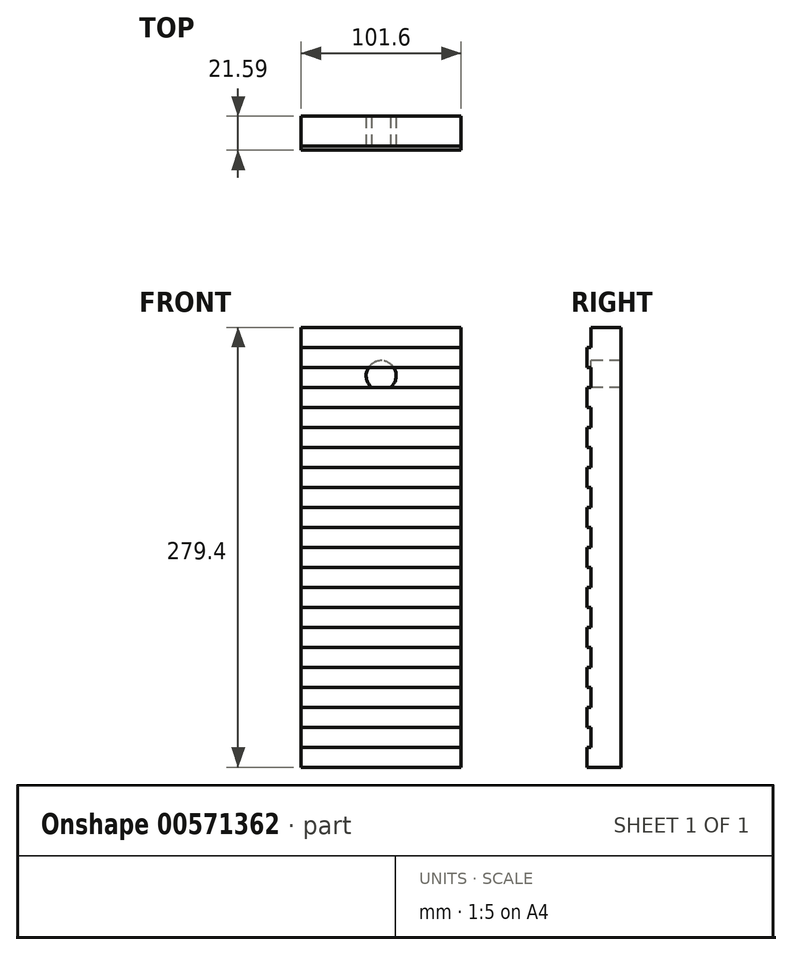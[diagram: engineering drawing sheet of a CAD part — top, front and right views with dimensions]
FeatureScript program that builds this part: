
annotation { "Feature Type Name" : "Feature", "Feature Type Description" : "" }
export const myFeature = defineFeature(function(context is Context, id is Id, definition is map)
    precondition{}
    {
        {
            var Q0;
            Q0=qCreatedBy(makeId("Front.planeOp"),FACE);
            var sketch = newSketch(context, id + "F0", { "sketchPlane" : qUnion([Q0])});
            skLineSegment(sketch, "E0", {"start": v(-129.55, 107.06) * mm, "end": v(-27.95, 107.06) * mm});
            skLineSegment(sketch, "E1", {"start": v(-27.95, 107.06) * mm, "end": v(-27.95, -172.34) * mm});
            skLineSegment(sketch, "E2", {"start": v(-27.95, -172.34) * mm, "end": v(-129.55, -172.34) * mm});
            skLineSegment(sketch, "E3", {"start": v(-129.55, 107.06) * mm, "end": v(-129.55, -172.34) * mm});
            skSolve(sketch);
        }
        {
            var Q0;
            Q0=makeQuery(id+"F0.imprint","IMPRINT",FACE,{"disambiguationData":[TD([[makeQuery(id+"F0.imprint","IMPRINT",EDGE,{"derivedFrom":sQuery(id+"F0.wireOp",EDGE,"E0")}),-1.0]])]});
            extrude(context, id + "F1", {"entities" : qUnion([Q0]), "depth" : 19.05 * mm, "offsetDistance" : 25.4 * mm});
        }
        {
            var Q0;
            Q0=makeQuery(id+"F1.opExtrude","CAP_FACE",FACE,{"disambiguationData":[OSD([sQuery(id+"F0.wireOp",EDGE,"E0"),sQuery(id+"F0.wireOp",EDGE,"E1"),sQuery(id+"F0.wireOp",EDGE,"E2"),sQuery(id+"F0.wireOp",EDGE,"E3")])],"isStart":false});
            var sketch = newSketch(context, id + "F2", { "sketchPlane" : qUnion([Q0])});
            skLineSegment(sketch, "E4.0", {"start": v(-129.55, 107.06) * mm, "end": v(-129.55, -172.34) * mm});
            skLineSegment(sketch, "E5.0", {"start": v(-129.55, 107.06) * mm, "end": v(-27.95, 107.06) * mm});
            skLineSegment(sketch, "E6.0", {"start": v(-27.95, -172.34) * mm, "end": v(-129.55, -172.34) * mm});
            skLineSegment(sketch, "E7.0", {"start": v(-27.95, 107.06) * mm, "end": v(-27.95, -172.34) * mm});
            skLineSegment(sketch, "E8", {"start": v(-129.55, -146.94) * mm, "end": v(-27.95, -146.94) * mm});
            skLineSegment(sketch, "E9", {"start": v(-129.55, -159.64) * mm, "end": v(-27.95, -159.64) * mm});
            skLineSegment(sketch, "E10", {"start": v(-129.55, -134.24) * mm, "end": v(-27.95, -134.24) * mm});
            skLineSegment(sketch, "E11", {"start": v(-129.55, -121.54) * mm, "end": v(-27.95, -121.54) * mm});
            skLineSegment(sketch, "E12", {"start": v(-129.55, -108.84) * mm, "end": v(-27.95, -108.84) * mm});
            skLineSegment(sketch, "E13", {"start": v(-129.55, -96.14) * mm, "end": v(-27.95, -96.14) * mm});
            skLineSegment(sketch, "E14", {"start": v(-129.55, -83.44) * mm, "end": v(-27.95, -83.44) * mm});
            skLineSegment(sketch, "E15", {"start": v(-129.55, -70.74) * mm, "end": v(-27.95, -70.74) * mm});
            skLineSegment(sketch, "E16", {"start": v(-129.55, -58.04) * mm, "end": v(-27.95, -58.04) * mm});
            skLineSegment(sketch, "E17", {"start": v(-129.55, -45.34) * mm, "end": v(-27.95, -45.34) * mm});
            skLineSegment(sketch, "E18", {"start": v(-129.55, -32.64) * mm, "end": v(-27.95, -32.64) * mm});
            skLineSegment(sketch, "E19", {"start": v(-129.55, -19.94) * mm, "end": v(-27.95, -19.94) * mm});
            skLineSegment(sketch, "E20", {"start": v(-129.55, -7.24) * mm, "end": v(-27.95, -7.24) * mm});
            skLineSegment(sketch, "E21", {"start": v(-129.55, 5.46) * mm, "end": v(-27.95, 5.46) * mm});
            skLineSegment(sketch, "E22", {"start": v(-129.55, 18.16) * mm, "end": v(-27.95, 18.16) * mm});
            skLineSegment(sketch, "E23", {"start": v(-129.55, 30.86) * mm, "end": v(-27.95, 30.86) * mm});
            skLineSegment(sketch, "E24", {"start": v(-129.55, 43.56) * mm, "end": v(-27.95, 43.56) * mm});
            skLineSegment(sketch, "E25", {"start": v(-129.55, 56.26) * mm, "end": v(-27.95, 56.26) * mm});
            skLineSegment(sketch, "E26", {"start": v(-129.55, 68.96) * mm, "end": v(-27.95, 68.96) * mm});
            skLineSegment(sketch, "E27", {"start": v(-129.55, 81.66) * mm, "end": v(-27.95, 81.66) * mm});
            skLineSegment(sketch, "E28", {"start": v(-129.55, 94.36) * mm, "end": v(-27.95, 94.36) * mm});
            skSolve(sketch);
        }
        {
            var Q0;
            {var subQ0=sQuery(id+"F2.wireOp",EDGE,"E11");Q0=makeQuery(id+"F2.imprint","IMPRINT",FACE,{"disambiguationData":[TD([[makeQuery(id+"F2.imprint","IMPRINT",EDGE,{"derivedFrom":subQ0}),1.0]])]});}
            var Q1;
            {var subQ0=sQuery(id+"F2.wireOp",EDGE,"E13");Q1=makeQuery(id+"F2.imprint","IMPRINT",FACE,{"disambiguationData":[TD([[makeQuery(id+"F2.imprint","IMPRINT",EDGE,{"derivedFrom":subQ0}),1.0]])]});}
            var Q2;
            {var subQ0=sQuery(id+"F2.wireOp",EDGE,"E15");Q2=makeQuery(id+"F2.imprint","IMPRINT",FACE,{"disambiguationData":[TD([[makeQuery(id+"F2.imprint","IMPRINT",EDGE,{"derivedFrom":subQ0}),1.0]])]});}
            var Q3;
            {var subQ0=sQuery(id+"F2.wireOp",EDGE,"E17");Q3=makeQuery(id+"F2.imprint","IMPRINT",FACE,{"disambiguationData":[TD([[makeQuery(id+"F2.imprint","IMPRINT",EDGE,{"derivedFrom":subQ0}),1.0]])]});}
            var Q4;
            {var subQ0=sQuery(id+"F2.wireOp",EDGE,"E19");Q4=makeQuery(id+"F2.imprint","IMPRINT",FACE,{"disambiguationData":[TD([[makeQuery(id+"F2.imprint","IMPRINT",EDGE,{"derivedFrom":subQ0}),1.0]])]});}
            var Q5;
            {var subQ0=sQuery(id+"F2.wireOp",EDGE,"E21");Q5=makeQuery(id+"F2.imprint","IMPRINT",FACE,{"disambiguationData":[TD([[makeQuery(id+"F2.imprint","IMPRINT",EDGE,{"derivedFrom":subQ0}),1.0]])]});}
            var Q6;
            {var subQ0=sQuery(id+"F2.wireOp",EDGE,"E23");Q6=makeQuery(id+"F2.imprint","IMPRINT",FACE,{"disambiguationData":[TD([[makeQuery(id+"F2.imprint","IMPRINT",EDGE,{"derivedFrom":subQ0}),1.0]])]});}
            var Q7;
            {var subQ0=sQuery(id+"F2.wireOp",EDGE,"E25");Q7=makeQuery(id+"F2.imprint","IMPRINT",FACE,{"disambiguationData":[TD([[makeQuery(id+"F2.imprint","IMPRINT",EDGE,{"derivedFrom":subQ0}),1.0]])]});}
            var Q8;
            {var subQ0=sQuery(id+"F2.wireOp",EDGE,"E27");Q8=makeQuery(id+"F2.imprint","IMPRINT",FACE,{"disambiguationData":[TD([[makeQuery(id+"F2.imprint","IMPRINT",EDGE,{"derivedFrom":subQ0}),1.0]])]});}
            var Q9;
            {var subQ0=sQuery(id+"F2.wireOp",EDGE,"E8");Q9=makeQuery(id+"F2.imprint","IMPRINT",FACE,{"disambiguationData":[TD([[makeQuery(id+"F2.imprint","IMPRINT",EDGE,{"derivedFrom":subQ0}),1.0]])]});}
            var Q10;
            {var subQ0=sQuery(id+"F2.wireOp",EDGE,"E6.0");Q10=makeQuery(id+"F2.imprint","IMPRINT",FACE,{"disambiguationData":[TD([[makeQuery(id+"F2.imprint","IMPRINT",EDGE,{"derivedFrom":subQ0}),-1.0]])]});}
            extrude(context, id + "F3", {"entities" : qUnion([Q0, Q1, Q2, Q3, Q4, Q5, Q6, Q7, Q8, Q9, Q10]), "operationType" : NewBodyOperationType.ADD, "depth" : 2.54 * mm, "offsetDistance" : 25.4 * mm});
        }
        {
            var Q0;
            {var subQ19=sQuery(id+"F2.wireOp",EDGE,"E26");var subQ20=sQuery(id+"F0.wireOp",EDGE,"E3");var subQ23=sQuery(id+"F0.wireOp",EDGE,"E1");Q0=makeQuery(id+"F3.boolean.opBoolean","SPLIT",FACE,{"disambiguationData":[TD([makeQuery(id+"F3.opExtrude","SWEPT_FACE",FACE,{"disambiguationData":[OSD([subQ19])]})])],"derivedFrom":makeQuery(id+"F1.opExtrude","CAP_FACE",FACE,{"disambiguationData":[OSD([sQuery(id+"F0.wireOp",EDGE,"E0"),subQ23,sQuery(id+"F0.wireOp",EDGE,"E2"),subQ20])],"isStart":false})});}
            var sketch = newSketch(context, id + "F4", { "sketchPlane" : qUnion([Q0])});
            skCircle(sketch, "E29", {"center": v(-78.75, 76.37) * mm, "radius": 9.53 * mm});
            skPoint(sketch, "E29.centerSnap0", {"position": v(-78.75, 68.96) * mm});
            skSolve(sketch);
        }
        {
            var Q0;
            {var subQ0=sQuery(id+"F4.wireOp",EDGE,"E29");var subQ1=makeQuery(id+"F3.opExtrude","CAP_EDGE",EDGE,{"disambiguationData":[OSD([sQuery(id+"F2.wireOp",EDGE,"E27")])],"isStart":true});var subQ2=makeQuery(id+"F4.imprint","INTERSECT",VERTEX,{"disambiguationData":[OD(0.0)],"derivedFrom":[subQ1,subQ0]});Q0=makeQuery(id+"F4.imprint","IMPRINT",FACE,{"disambiguationData":[TD([[makeQuery(id+"F4.imprint","IMPRINT",EDGE,{"disambiguationData":[TD([[subQ2,1.0]])],"derivedFrom":subQ0}),1.0]])]});}
            var Q1;
            {var subQ0=sQuery(id+"F4.wireOp",EDGE,"E29");var subQ1=makeQuery(id+"F3.opExtrude","CAP_EDGE",EDGE,{"disambiguationData":[OSD([sQuery(id+"F2.wireOp",EDGE,"E26")])],"isStart":true});var subQ2=makeQuery(id+"F4.imprint","INTERSECT",VERTEX,{"disambiguationData":[OD(0.0)],"derivedFrom":[subQ1,subQ0]});Q1=makeQuery(id+"F4.imprint","IMPRINT",FACE,{"disambiguationData":[TD([[makeQuery(id+"F4.imprint","IMPRINT",EDGE,{"disambiguationData":[TD([[subQ2,-1.0]])],"derivedFrom":subQ0}),1.0]])]});}
            var Q2;
            {var subQ0=sQuery(id+"F4.wireOp",EDGE,"E29");var subQ1=makeQuery(id+"F3.opExtrude","CAP_EDGE",EDGE,{"disambiguationData":[OSD([sQuery(id+"F2.wireOp",EDGE,"E27")])],"isStart":true});var subQ2=makeQuery(id+"F4.imprint","INTERSECT",VERTEX,{"disambiguationData":[OD(0.0)],"derivedFrom":[subQ1,subQ0]});Q2=makeQuery(id+"F4.imprint","IMPRINT",FACE,{"disambiguationData":[TD([[makeQuery(id+"F4.imprint","IMPRINT",EDGE,{"disambiguationData":[TD([[subQ2,-1.0]])],"derivedFrom":subQ0}),1.0]])]});}
            extrude(context, id + "F5", {"entities" : qUnion([Q0, Q1, Q2]), "operationType" : NewBodyOperationType.REMOVE, "oppositeDirection" : true, "depth" : 25.4 * mm, "offsetDistance" : 25.4 * mm});
        }
    });
